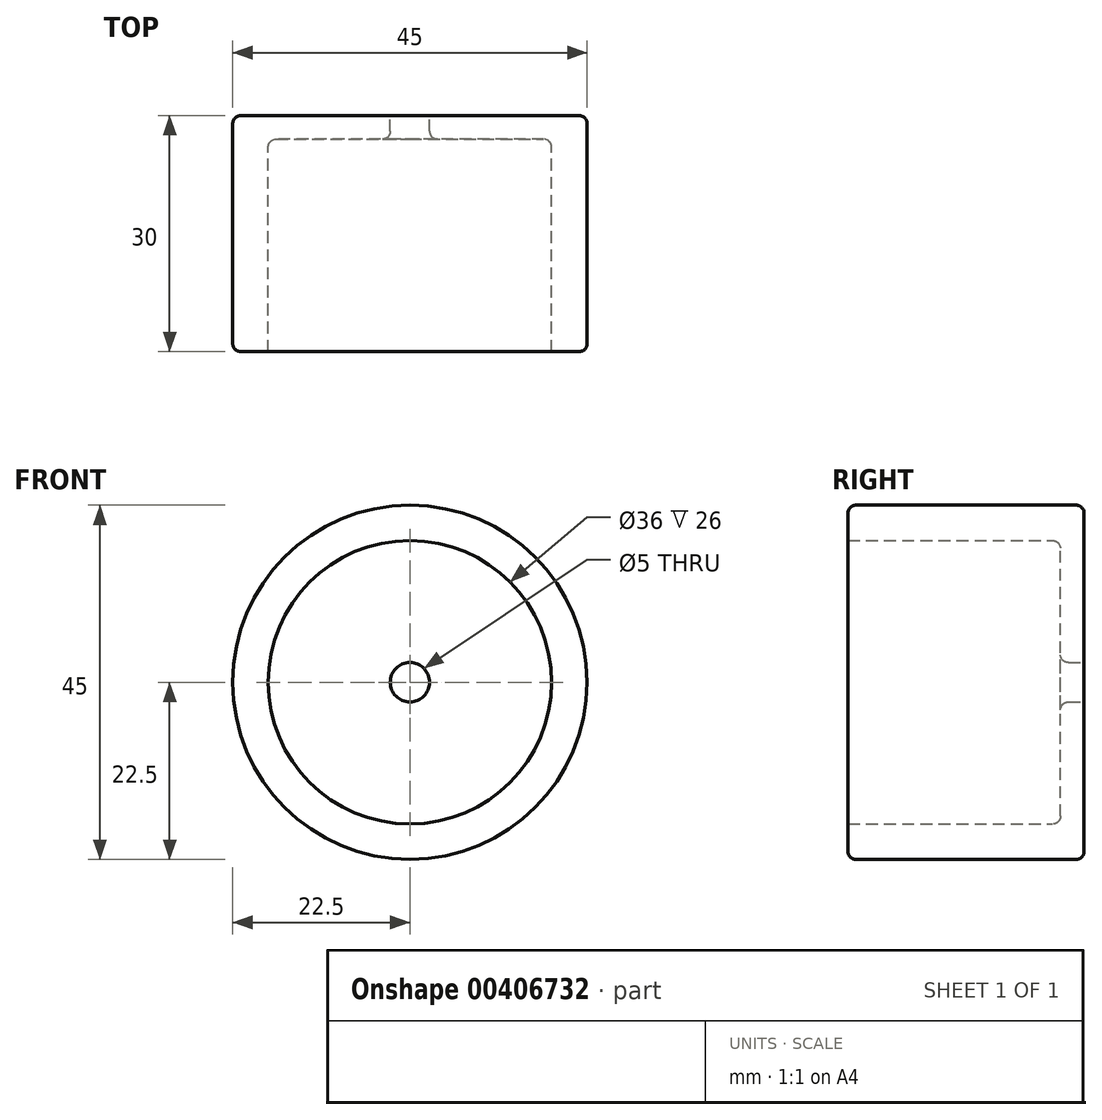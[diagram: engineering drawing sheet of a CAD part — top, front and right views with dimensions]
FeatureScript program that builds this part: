
annotation { "Feature Type Name" : "Feature", "Feature Type Description" : "" }
export const myFeature = defineFeature(function(context is Context, id is Id, definition is map)
    precondition{}
    {
        {
            var Q0;
            Q0=qCreatedBy(makeId("Front.planeOp"),FACE);
            var sketch = newSketch(context, id + "F0", { "sketchPlane" : qUnion([Q0])});
            skCircle(sketch, "E0", {"center": v(0, 0) * mm, "radius": 22.5 * mm});
            skCircle(sketch, "E1", {"center": v(0, 0) * mm, "radius": 18 * mm});
            skSolve(sketch);
        }
        {
            var Q0;
            Q0=makeQuery(id+"F0.imprint","IMPRINT",FACE,{"disambiguationData":[TD([[makeQuery(id+"F0.imprint","IMPRINT",EDGE,{"derivedFrom":sQuery(id+"F0.wireOp",EDGE,"E1")}),1.0]])]});
            var Q1;
            Q1=makeQuery(id+"F0.imprint","IMPRINT",FACE,{"disambiguationData":[TD([[makeQuery(id+"F0.imprint","IMPRINT",EDGE,{"derivedFrom":sQuery(id+"F0.wireOp",EDGE,"E0")}),1.0]])]});
            extrude(context, id + "F1", {"entities" : qUnion([Q0, Q1]), "depth" : 3 * mm});
        }
        {
            var Q0;
            Q0=makeQuery(id+"F0.imprint","IMPRINT",FACE,{"disambiguationData":[TD([[makeQuery(id+"F0.imprint","IMPRINT",EDGE,{"derivedFrom":sQuery(id+"F0.wireOp",EDGE,"E0")}),1.0]])]});
            extrude(context, id + "F2", {"entities" : qUnion([Q0]), "operationType" : NewBodyOperationType.ADD, "depth" : 30 * mm});
        }
        {
            var Q0;
            Q0=makeQuery(id+"F2.boolean.opBoolean","INTERSECT",EDGE,{"derivedFrom":[makeQuery(id+"F1.opExtrude","CAP_FACE",FACE,{"disambiguationData":[OSD([sQuery(id+"F0.wireOp",EDGE,"E0")])],"isStart":false}),makeQuery(id+"F2.opExtrude","SWEPT_FACE",FACE,{"disambiguationData":[OSD([sQuery(id+"F0.wireOp",EDGE,"E1")])]})]});
            var Q1;
            Q1=makeQuery(id+"F2.opExtrude","CAP_EDGE",EDGE,{"disambiguationData":[OSD([sQuery(id+"F0.wireOp",EDGE,"E0")])],"isStart":false});
            var Q2;
            Q2=makeQuery(id+"F1.opExtrude","CAP_EDGE",EDGE,{"disambiguationData":[OSD([sQuery(id+"F0.wireOp",EDGE,"E0")])],"isStart":true});
            fillet(context, id + "F3", {"entities" : qUnion([Q0, Q1, Q2]), "radius" : 1 * mm, "tangentPropagation" : true, "allowEdgeOverflow" : false});
        }
        {
            var Q0;
            Q0=makeQuery(id+"F1.opExtrude","CAP_FACE",FACE,{"disambiguationData":[OSD([sQuery(id+"F0.wireOp",EDGE,"E0")])],"isStart":true});
            var sketch = newSketch(context, id + "F4", { "sketchPlane" : qUnion([Q0])});
            skCircle(sketch, "E2", {"center": v(0, 0) * mm, "radius": 2.5 * mm});
            skSolve(sketch);
        }
        {
            var Q0;
            Q0 = qSketchRegion(id + "F4", true);
            var Q1;
            Q1=makeQuery(id+"F4.imprint","IMPRINT",FACE,{"disambiguationData":[TD([[makeQuery(id+"F4.imprint","IMPRINT",EDGE,{"derivedFrom":sQuery(id+"F4.wireOp",EDGE,"E2")}),1.0]])]});
            extrude(context, id + "F5", {"entities" : qUnion([Q0, Q1]), "operationType" : NewBodyOperationType.REMOVE, "oppositeDirection" : true, "depth" : 25 * mm});
        }
        {
            var Q0;
            Q0=makeQuery(id+"F5.boolean.opBoolean","INTERSECT",EDGE,{"derivedFrom":[makeQuery(id+"F1.opExtrude","CAP_FACE",FACE,{"disambiguationData":[OSD([sQuery(id+"F0.wireOp",EDGE,"E0")])],"isStart":false}),makeQuery(id+"F5.opExtrude","SWEPT_FACE",FACE,{"disambiguationData":[OSD([sQuery(id+"F4.wireOp",EDGE,"E2")])]})]});
            var Q1;
            Q1=makeQuery(id+"F5.boolean.opBoolean","COPY",EDGE,{"derivedFrom":makeQuery(id+"F5.opExtrude","CAP_EDGE",EDGE,{"disambiguationData":[OSD([sQuery(id+"F4.wireOp",EDGE,"E2")])],"isStart":true})});
            fillet(context, id + "F6", {"entities" : qUnion([Q0, Q1]), "radius" : 1 * mm, "tangentPropagation" : true, "allowEdgeOverflow" : false});
        }
    });
